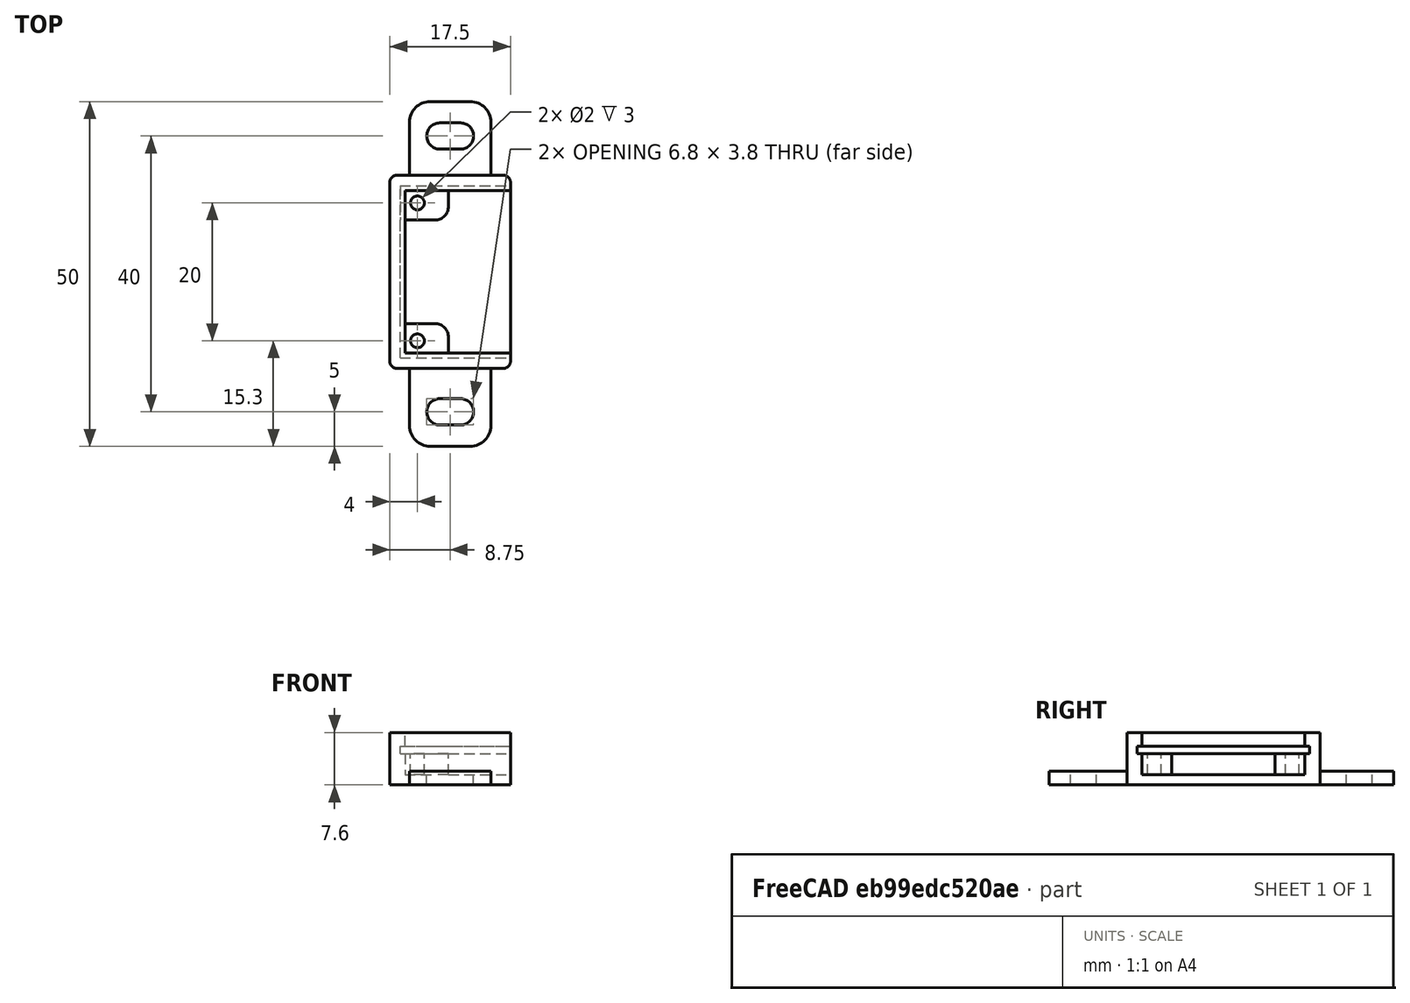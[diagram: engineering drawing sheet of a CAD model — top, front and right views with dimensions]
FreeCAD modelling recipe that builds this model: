
FCSTD DOCUMENT  (FreeCAD 0.19R)
Label: amplifier_pam8403
License: FreeArt
LicenseURL: http://artlibre.org/licence/lal
objects: Part::Box×4, Part::MultiFuse×4, Part::Fillet×2, Part::Cut×2, Spreadsheet::Sheet×1, Part::Cylinder×1, Part::Mirroring×1, Part::Feature×1, App::Part×1
note: 15 computed .brp shape members not serialized (recipe doc carries the construction recipe); baked Part::Feature solids carry a one-line shape summary decoded from their .brp

FEATURE [Spreadsheet::Sheet] Spreadsheet  label="p"
  cells = A1=pcb_x; B1(pcb_x)=16; A2=pcb_y; B2(pcb_y)=25; A3=pcb_z; B3(pcb_z)=1.1; A4=pcb_under; B4(pcb_under)=3; A5=side_wall; B5(side_wall)=1.5; A6=pcb_side_lane; B6(pcb_side_lane)=0.7; A7=bottom_wall; B7(bottom_wall)=1.5; A8=pcb_above; B8(pcb_above)=2; A9=hole_dist_y; B9(hole_dist_y)=20; A10=hole_off_x; B10(hole_off_x)=2.5; A11=hole_r; B11(hole_r)=1; A12=hole_stand_x; B12(hole_stand_x)=7; A13=hole_stand_y; B13(hole_stand_y)=5
FEATURE [Part::Box] Box  label="external cube"
  AttacherType = Attacher::AttachEngine3D
  Height = 7.6
  Length = 17.5
  Width = 28
  expr: Height = <<p>>.bottom_wall + <<p>>.pcb_under + <<p>>.pcb_z + <<p>>.pcb_above
  expr: Width = <<p>>.pcb_y + 2 * <<p>>.side_wall
  expr: Length = <<p>>.pcb_x + <<p>>.side_wall
FEATURE [Part::Box] Box006  label="internal cube"
  AttacherType = Attacher::AttachEngine3D
  Height = 6.1
  Length = 16.1
  Placement = pos=(2.2,2.2,1.5) rot=(0,0,1;0rad)
  Width = 23.6
  expr: .Placement.Base.y = <<p>>.side_wall + <<p>>.pcb_side_lane
  expr: .Placement.Base.x = <<p>>.side_wall + <<p>>.pcb_side_lane
  expr: .Placement.Base.z = <<p>>.bottom_wall
  expr: Height = <<p>>.pcb_under + <<p>>.pcb_z + <<p>>.pcb_above
  expr: Width = <<p>>.pcb_y - 2 * <<p>>.pcb_side_lane
  expr: Length = <<p>>.pcb_x - 2 * <<p>>.pcb_side_lane + <<p>>.side_wall
FEATURE [Part::Box] Box007  label="pcb extract cube"
  AttacherType = Attacher::AttachEngine3D
  Height = 1.1
  Length = 16
  Placement = pos=(1.5,1.5,4.5) rot=(0,0,1;0rad)
  Width = 25
  expr: .Placement.Base.y = <<p>>.side_wall
  expr: .Placement.Base.x = <<p>>.side_wall
  expr: Length = <<p>>.pcb_x
  expr: Width = <<p>>.pcb_y
  expr: .Placement.Base.z = <<p>>.bottom_wall + <<p>>.pcb_under
  expr: Height = <<p>>.pcb_z
FEATURE [Part::MultiFuse] Fusion  label="extract fusion"
  Shapes = -> [Box006,Box007]
FEATURE [Part::Fillet] Fillet  label="external fillet"
  Base = -> Box
  Edges = 4 edges r=1: [Edge1,Edge3,Edge5,Edge7]
FEATURE [Part::Box] Box008  label="hole stand"
  AttacherType = Attacher::AttachEngine3D
  Height = 3
  Length = 7
  Placement = pos=(1.5,1.5,1.5) rot=(0,0,1;0rad)
  Width = 5
  expr: .Placement.Base.x = <<p>>.side_wall
  expr: .Placement.Base.y = <<p>>.side_wall
  expr: Length = <<p>>.hole_stand_x
  expr: Width = <<p>>.hole_stand_y
  expr: .Placement.Base.z = <<p>>.bottom_wall
  expr: Height = <<p>>.pcb_under
FEATURE [Part::Cylinder] Cylinder  label="hole"
  Angle = 360
  AttacherType = Attacher::AttachEngine3D
  Height = 10
  Placement = pos=(4,4,0) rot=(0,0,1;0rad)
  Radius = 1
  expr: .Placement.Base.y = <<p>>.side_wall + (<<p>>.pcb_y - <<p>>.hole_dist_y) / 2
  expr: .Placement.Base.x = <<p>>.hole_off_x + <<p>>.side_wall
  expr: Radius = <<p>>.hole_r
FEATURE [Part::Fillet] Fillet001  label="hole stand fillet"
  Base = -> Box008
  Edges = 1 edges r=2: [Edge7]
FEATURE [Part::Cut] Cut002003  label="hole cut"
  Base = -> Fillet001
  Tool = -> Cylinder
FEATURE [Part::Mirroring] Part__Mirroring  label="hole stand (Mirror #1)"
  Base = (0,14,0)
  Normal = (0,1,0)
  Source = -> Cut002003
  expr: .Base.y = <<p>>.pcb_y / 2 + <<p>>.side_wall
FEATURE [Part::MultiFuse] Fusion002  label="hole fusion"
  Shapes = -> [Cut002003,Part__Mirroring]
FEATURE [Part::Feature] Cut002001  label="attach plane y dir001"
  Placement = pos=(2.85,-11.3,0) rot=(0,0,1;0rad)
  shape: bbox 11.8 x 50 x 2 mm, 20 faces (baked)
FEATURE [Part::MultiFuse] Fusion001  label="solid fusion"
  Shapes = -> [Fillet,Cut002001]
FEATURE [Part::Cut] Cut  label="sd card cut"
  Base = -> Fusion001
  Tool = -> Fusion
FEATURE [Part::MultiFuse] Fusion003  label="box fusion"
  Shapes = -> [Fusion002,Cut]
FEATURE [App::Part] Part  label="pcb box part"
  Group = -> [Box,Fillet,Fusion001,Fusion,Box007,Box006,Cut,Part__Mirroring,Cut002003,Fusion002,Box008,Fillet001,Cylinder,Fusion003]
  Origin = -> Origin
